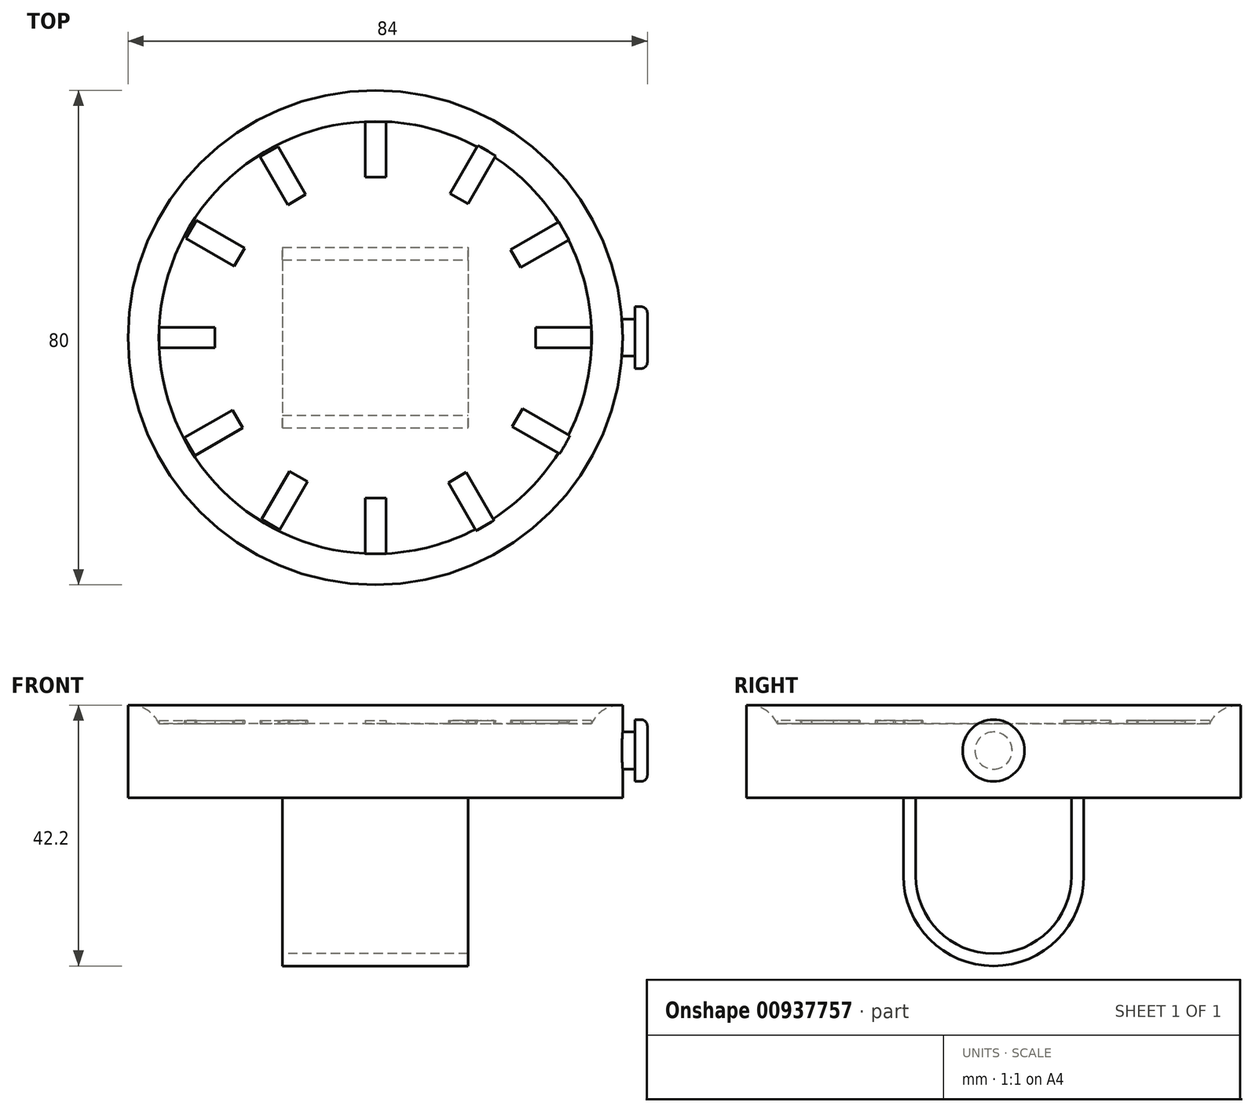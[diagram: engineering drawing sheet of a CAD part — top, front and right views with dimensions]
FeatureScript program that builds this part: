
annotation { "Feature Type Name" : "Feature", "Feature Type Description" : "" }
export const myFeature = defineFeature(function(context is Context, id is Id, definition is map)
    precondition{}
    {
        {
            var Q0;
            Q0=qCreatedBy(makeId("Top.planeOp"),FACE);
            var sketch = newSketch(context, id + "F0", { "sketchPlane" : qUnion([Q0])});
            skCircle(sketch, "E0", {"center": v(0, 0) * mm, "radius": 40 * mm});
            skCircle(sketch, "E1", {"center": v(0, 0) * mm, "radius": 35 * mm});
            skSolve(sketch);
        }
        {
            var Q0;
            Q0=makeQuery(id+"F0.imprint","IMPRINT",FACE,{"disambiguationData":[TD([[makeQuery(id+"F0.imprint","IMPRINT",EDGE,{"derivedFrom":sQuery(id+"F0.wireOp",EDGE,"E0")}),1.0]])]});
            extrude(context, id + "F1", {"entities" : qUnion([Q0]), "depth" : 15 * mm, "offsetDistance" : 25 * mm});
        }
        {
            var Q0;
            Q0=qCreatedBy(makeId("Top.planeOp"),FACE);
            var sketch = newSketch(context, id + "F2", { "sketchPlane" : qUnion([Q0])});
            skCircle(sketch, "E2", {"center": v(0, 0) * mm, "radius": 35 * mm});
            skSolve(sketch);
        }
        {
            var Q0;
            Q0=qSketchRegion(id+"F2",true);
            extrude(context, id + "F3", {"entities" : qUnion([Q0]), "operationType" : NewBodyOperationType.ADD, "depth" : 12 * mm, "offsetDistance" : 25 * mm});
        }
        {
            var Q0;
            Q0=makeQuery(id+"F1.opExtrude","CAP_EDGE",EDGE,{"disambiguationData":[OSD([sQuery(id+"F0.wireOp",EDGE,"E1")])],"isStart":false});
            fillet(context, id + "F4", {"entities" : qUnion([Q0]), "radius" : 5 * mm, "tangentPropagation" : true, "allowEdgeOverflow" : false});
        }
        {
            var Q0;
            Q0=qCreatedBy(makeId("Right.planeOp"),FACE);
            var sketch = newSketch(context, id + "F5", { "sketchPlane" : qUnion([Q0])});
            skCircle(sketch, "E3", {"center": v(0, 7.67) * mm, "radius": 3 * mm});
            skSolve(sketch);
        }
        {
            var Q0;
            Q0=qSketchRegion(id+"F5",true);
            extrude(context, id + "F6", {"entities" : qUnion([Q0]), "operationType" : NewBodyOperationType.ADD, "depth" : 42 * mm, "offsetDistance" : 25 * mm});
        }
        {
            var Q0;
            Q0=makeQuery(id+"F6.opExtrude","CAP_FACE",FACE,{"disambiguationData":[OSD([sQuery(id+"F5.wireOp",EDGE,"E3")])],"isStart":false});
            var sketch = newSketch(context, id + "F7", { "sketchPlane" : qUnion([Q0])});
            skCircle(sketch, "E4", {"center": v(0, 7.67) * mm, "radius": 5 * mm});
            skSolve(sketch);
        }
        {
            var Q0;
            Q0=qSketchRegion(id+"F7",true);
            extrude(context, id + "F8", {"entities" : qUnion([Q0]), "operationType" : NewBodyOperationType.ADD, "depth" : 2 * mm, "offsetDistance" : 25 * mm});
        }
        {
            var Q0;
            Q0=makeQuery(id+"F8.opExtrude","CAP_EDGE",EDGE,{"disambiguationData":[OSD([sQuery(id+"F7.wireOp",EDGE,"E4")])],"isStart":false});
            fillet(context, id + "F9", {"entities" : qUnion([Q0]), "radius" : 1 * mm, "tangentPropagation" : true, "allowEdgeOverflow" : false});
        }
        {
            var Q0;
            Q0=makeQuery(id+"F3.boolean.opBoolean","MERGE",FACE,{"derivedFrom":[makeQuery(id+"F1.opExtrude","CAP_FACE",FACE,{"disambiguationData":[OSD([sQuery(id+"F0.wireOp",EDGE,"E0"),sQuery(id+"F0.wireOp",EDGE,"E1")])],"isStart":true}),makeQuery(id+"F3.opExtrude","CAP_FACE",FACE,{"disambiguationData":[OSD([sQuery(id+"F2.wireOp",EDGE,"E2")])],"isStart":true})]});
            var sketch = newSketch(context, id + "F10", { "sketchPlane" : qUnion([Q0])});
            skLineSegment(sketch, "E5.bottom", {"start": v(15, 13) * mm, "end": v(-15, 13) * mm});
            skLineSegment(sketch, "E5.top", {"start": v(15, -13) * mm, "end": v(-15, -13) * mm});
            skLineSegment(sketch, "E5.left", {"start": v(15, 13) * mm, "end": v(15, -13) * mm});
            skLineSegment(sketch, "E5.right", {"start": v(-15, 13) * mm, "end": v(-15, -13) * mm});
            skPoint(sketch, "E5.middle", {"position": v(0, 0) * mm});
            skSolve(sketch);
        }
        {
            var Q0;
            Q0=makeQuery(id+"F3.opExtrude","CAP_FACE",FACE,{"disambiguationData":[OSD([sQuery(id+"F2.wireOp",EDGE,"E2")])],"isStart":false});
            var sketch = newSketch(context, id + "F11", { "sketchPlane" : qUnion([Q0])});
            skLineSegment(sketch, "E6.bottom", {"start": v(34.96, 1.68) * mm, "end": v(25.96, 1.68) * mm});
            skLineSegment(sketch, "E6.top", {"start": v(34.96, -1.68) * mm, "end": v(25.96, -1.68) * mm});
            skLineSegment(sketch, "E6.left", {"start": v(34.96, 1.68) * mm, "end": v(34.96, -1.68) * mm});
            skLineSegment(sketch, "E6.right", {"start": v(25.96, 1.68) * mm, "end": v(25.96, -1.68) * mm});
            skPoint(sketch, "E6.middle", {"position": v(30.46, 0) * mm});
            skLineSegment(sketch, "E7.MirrorCS", {"start": v(-34.96, 1.68) * mm, "end": v(-25.96, 1.68) * mm});
            skLineSegment(sketch, "E8.MirrorCS", {"start": v(-25.96, 1.68) * mm, "end": v(-25.96, -1.68) * mm});
            skLineSegment(sketch, "E9.MirrorCS", {"start": v(-34.96, -1.68) * mm, "end": v(-25.96, -1.68) * mm});
            skLineSegment(sketch, "E10.MirrorCS", {"start": v(-34.96, 1.68) * mm, "end": v(-34.96, -1.68) * mm});
            skLineSegment(sketch, "E11.MirrorCS", {"start": v(-1.61, 34.96) * mm, "end": v(1.74, 34.96) * mm});
            skLineSegment(sketch, "E12", {"start": v(-1.61, 34.96) * mm, "end": v(-1.61, 25.96) * mm});
            skLineSegment(sketch, "E13", {"start": v(-1.61, 25.96) * mm, "end": v(1.74, 25.96) * mm});
            skLineSegment(sketch, "E14", {"start": v(1.74, 25.96) * mm, "end": v(1.74, 34.96) * mm});
            skLineSegment(sketch, "E15.MirrorCS", {"start": v(1.74, 43.96) * mm, "end": v(1.74, 34.96) * mm});
            skLineSegment(sketch, "E16.MirrorCS", {"start": v(-1.61, 34.96) * mm, "end": v(-1.61, 43.96) * mm});
            skLineSegment(sketch, "E17.MirrorCS", {"start": v(-1.61, -25.96) * mm, "end": v(1.74, -25.96) * mm});
            skLineSegment(sketch, "E18.MirrorCS", {"start": v(-1.61, -34.96) * mm, "end": v(-1.61, -25.96) * mm});
            skLineSegment(sketch, "E19.MirrorCS", {"start": v(1.74, -25.96) * mm, "end": v(1.74, -34.96) * mm});
            skLineSegment(sketch, "E20.MirrorCS", {"start": v(-1.61, -34.96) * mm, "end": v(1.74, -34.96) * mm});
            skLineSegment(sketch, "E21.bottom", {"start": v(31.61, -15.98) * mm, "end": v(23.82, -11.48) * mm});
            skLineSegment(sketch, "E21.top", {"start": v(29.94, -18.88) * mm, "end": v(22.14, -14.38) * mm});
            skLineSegment(sketch, "E21.left", {"start": v(31.61, -15.98) * mm, "end": v(29.94, -18.88) * mm});
            skLineSegment(sketch, "E21.right", {"start": v(23.82, -11.48) * mm, "end": v(22.14, -14.38) * mm});
            skPoint(sketch, "E21.middle", {"position": v(26.88, -15.18) * mm});
            skLineSegment(sketch, "E22.MirrorCS", {"start": v(-28.94, 18.98) * mm, "end": v(-21.15, 14.48) * mm});
            skLineSegment(sketch, "E23.MirrorCS", {"start": v(-21.15, 14.48) * mm, "end": v(-22.82, 11.58) * mm});
            skLineSegment(sketch, "E24.MirrorCS", {"start": v(-30.62, 16.08) * mm, "end": v(-22.82, 11.58) * mm});
            skLineSegment(sketch, "E25.MirrorCS", {"start": v(-28.94, 18.98) * mm, "end": v(-30.62, 16.08) * mm});
            skLineSegment(sketch, "E26.MirrorCS", {"start": v(16.58, 31.13) * mm, "end": v(19.48, 29.45) * mm});
            skLineSegment(sketch, "E27", {"start": v(16.58, 31.13) * mm, "end": v(12.08, 23.33) * mm});
            skLineSegment(sketch, "E28", {"start": v(12.08, 23.33) * mm, "end": v(14.98, 21.66) * mm});
            skLineSegment(sketch, "E29", {"start": v(14.98, 21.66) * mm, "end": v(19.48, 29.45) * mm});
            skLineSegment(sketch, "E30.MirrorCS", {"start": v(23.98, 37.24) * mm, "end": v(19.48, 29.45) * mm});
            skLineSegment(sketch, "E31.MirrorCS", {"start": v(16.58, 31.13) * mm, "end": v(21.08, 38.92) * mm});
            skLineSegment(sketch, "E32.MirrorCS", {"start": v(-13.88, -21.63) * mm, "end": v(-10.98, -23.3) * mm});
            skLineSegment(sketch, "E33.MirrorCS", {"start": v(-18.38, -29.42) * mm, "end": v(-13.88, -21.63) * mm});
            skLineSegment(sketch, "E34.MirrorCS", {"start": v(-10.98, -23.3) * mm, "end": v(-15.48, -31.1) * mm});
            skLineSegment(sketch, "E35.MirrorCS", {"start": v(-18.38, -29.42) * mm, "end": v(-15.48, -31.1) * mm});
            skLineSegment(sketch, "E36.0", {"start": v(14.98, 21.66) * mm, "end": v(19.48, 29.45) * mm, "construction": true});
            skLineSegment(sketch, "E37.bottom", {"start": v(29.66, 18.75) * mm, "end": v(21.87, 14.25) * mm});
            skLineSegment(sketch, "E37.top", {"start": v(31.34, 15.84) * mm, "end": v(23.54, 11.34) * mm});
            skLineSegment(sketch, "E37.left", {"start": v(29.66, 18.75) * mm, "end": v(31.34, 15.84) * mm});
            skLineSegment(sketch, "E37.right", {"start": v(21.87, 14.25) * mm, "end": v(23.54, 11.34) * mm});
            skPoint(sketch, "E37.middle", {"position": v(26.6, 15.04) * mm});
            skLineSegment(sketch, "E38.MirrorCS", {"start": v(-30.9, -16.21) * mm, "end": v(-23.1, -11.71) * mm});
            skLineSegment(sketch, "E39.MirrorCS", {"start": v(-23.1, -11.71) * mm, "end": v(-21.42, -14.62) * mm});
            skLineSegment(sketch, "E40.MirrorCS", {"start": v(-29.22, -19.12) * mm, "end": v(-21.42, -14.62) * mm});
            skLineSegment(sketch, "E41.MirrorCS", {"start": v(-30.9, -16.21) * mm, "end": v(-29.22, -19.12) * mm});
            skLineSegment(sketch, "E42.MirrorCS", {"start": v(-18.65, 29.28) * mm, "end": v(-15.75, 30.96) * mm});
            skLineSegment(sketch, "E43", {"start": v(-18.65, 29.28) * mm, "end": v(-14.15, 21.49) * mm});
            skLineSegment(sketch, "E44", {"start": v(-14.15, 21.49) * mm, "end": v(-11.25, 23.16) * mm});
            skLineSegment(sketch, "E45", {"start": v(-11.25, 23.16) * mm, "end": v(-15.75, 30.96) * mm});
            skLineSegment(sketch, "E46.MirrorCS", {"start": v(-20.25, 38.75) * mm, "end": v(-15.75, 30.96) * mm});
            skLineSegment(sketch, "E47.MirrorCS", {"start": v(-18.65, 29.28) * mm, "end": v(-23.15, 37.08) * mm});
            skLineSegment(sketch, "E48.MirrorCS", {"start": v(11.8, -23.47) * mm, "end": v(14.7, -21.8) * mm});
            skLineSegment(sketch, "E49.MirrorCS", {"start": v(16.3, -31.26) * mm, "end": v(11.8, -23.47) * mm});
            skLineSegment(sketch, "E50.MirrorCS", {"start": v(14.7, -21.8) * mm, "end": v(19.2, -29.59) * mm});
            skLineSegment(sketch, "E51.MirrorCS", {"start": v(16.3, -31.26) * mm, "end": v(19.2, -29.59) * mm});
            skLineSegment(sketch, "E52.0", {"start": v(-11.25, 23.16) * mm, "end": v(-15.75, 30.96) * mm, "construction": true});
            skSolve(sketch);
        }
        {
            var Q0;
            Q0=qSketchRegion(id+"F11",true);
            extrude(context, id + "F12", {"entities" : qUnion([Q0]), "operationType" : NewBodyOperationType.ADD, "depth" : 0.5 * mm, "offsetDistance" : 25 * mm});
        }
        {
            var Q0;
            Q0=makeQuery(id+"F10.imprint","IMPRINT",FACE,{"disambiguationData":[TD([[makeQuery(id+"F10.imprint","IMPRINT",EDGE,{"derivedFrom":sQuery(id+"F10.wireOp",EDGE,"E5.bottom")}),-1.0]])]});
            var sketch = newSketch(context, id + "F13", { "sketchPlane" : qUnion([Q0])});
            skLineSegment(sketch, "E53.bottom", {"start": v(-15, -12.6) * mm, "end": v(15, -12.6) * mm});
            skLineSegment(sketch, "E53.top", {"start": v(-15, -14.6) * mm, "end": v(15, -14.6) * mm});
            skLineSegment(sketch, "E53.left", {"start": v(-15, -12.6) * mm, "end": v(-15, -14.6) * mm});
            skLineSegment(sketch, "E53.right", {"start": v(15, -12.6) * mm, "end": v(15, -14.6) * mm});
            skLineSegment(sketch, "E54.bottom", {"start": v(-15, 14.6) * mm, "end": v(15, 14.6) * mm});
            skLineSegment(sketch, "E54.top", {"start": v(-15, 12.6) * mm, "end": v(15, 12.6) * mm});
            skLineSegment(sketch, "E54.left", {"start": v(-15, 14.6) * mm, "end": v(-15, 12.6) * mm});
            skLineSegment(sketch, "E54.right", {"start": v(15, 14.6) * mm, "end": v(15, 12.6) * mm});
            skSolve(sketch);
        }
        {
            var Q0;
            Q0=qSketchRegion(id+"F13",true);
            extrude(context, id + "F14", {"entities" : qUnion([Q0]), "operationType" : NewBodyOperationType.ADD, "depth" : 12.6 * mm, "offsetDistance" : 25 * mm});
        }
        {
            var Q0;
            Q0=makeQuery(id+"F14.opExtrude","CAP_FACE",FACE,{"disambiguationData":[OSD([sQuery(id+"F13.wireOp",EDGE,"E54.bottom"),sQuery(id+"F13.wireOp",EDGE,"E54.top"),sQuery(id+"F13.wireOp",EDGE,"E54.left"),sQuery(id+"F13.wireOp",EDGE,"E54.right")])],"isStart":false});
            var sketch = newSketch(context, id + "F15", { "sketchPlane" : qUnion([Q0])});
            skLineSegment(sketch, "E55", {"start": v(-30.75, 0) * mm, "end": v(30.75, 0) * mm});
            skSolve(sketch);
        }
        {
            var Q0;
            Q0=makeQuery(id+"F15.imprint","IMPRINT",FACE,{"disambiguationData":[TD([[makeQuery(id+"F15.imprint","IMPRINT",EDGE,{"derivedFrom":makeQuery(id+"F14.opExtrude","CAP_EDGE",EDGE,{"disambiguationData":[OSD([sQuery(id+"F13.wireOp",EDGE,"E54.bottom")])],"isStart":false})}),-1.0]])]});
            var Q1;
            Q1=sQuery(id+"F15.wireOp",EDGE,"E55");
            revolve(context, id + "F16", {"operationType" : NewBodyOperationType.ADD, "surfaceOperationType" : NewSurfaceOperationType.NEW, "entities" : qUnion([Q0]), "axis" : qUnion([Q1]), "revolveType" : RevolveType.ONE_DIRECTION, "angle" : 180 * degree});
        }
    });
